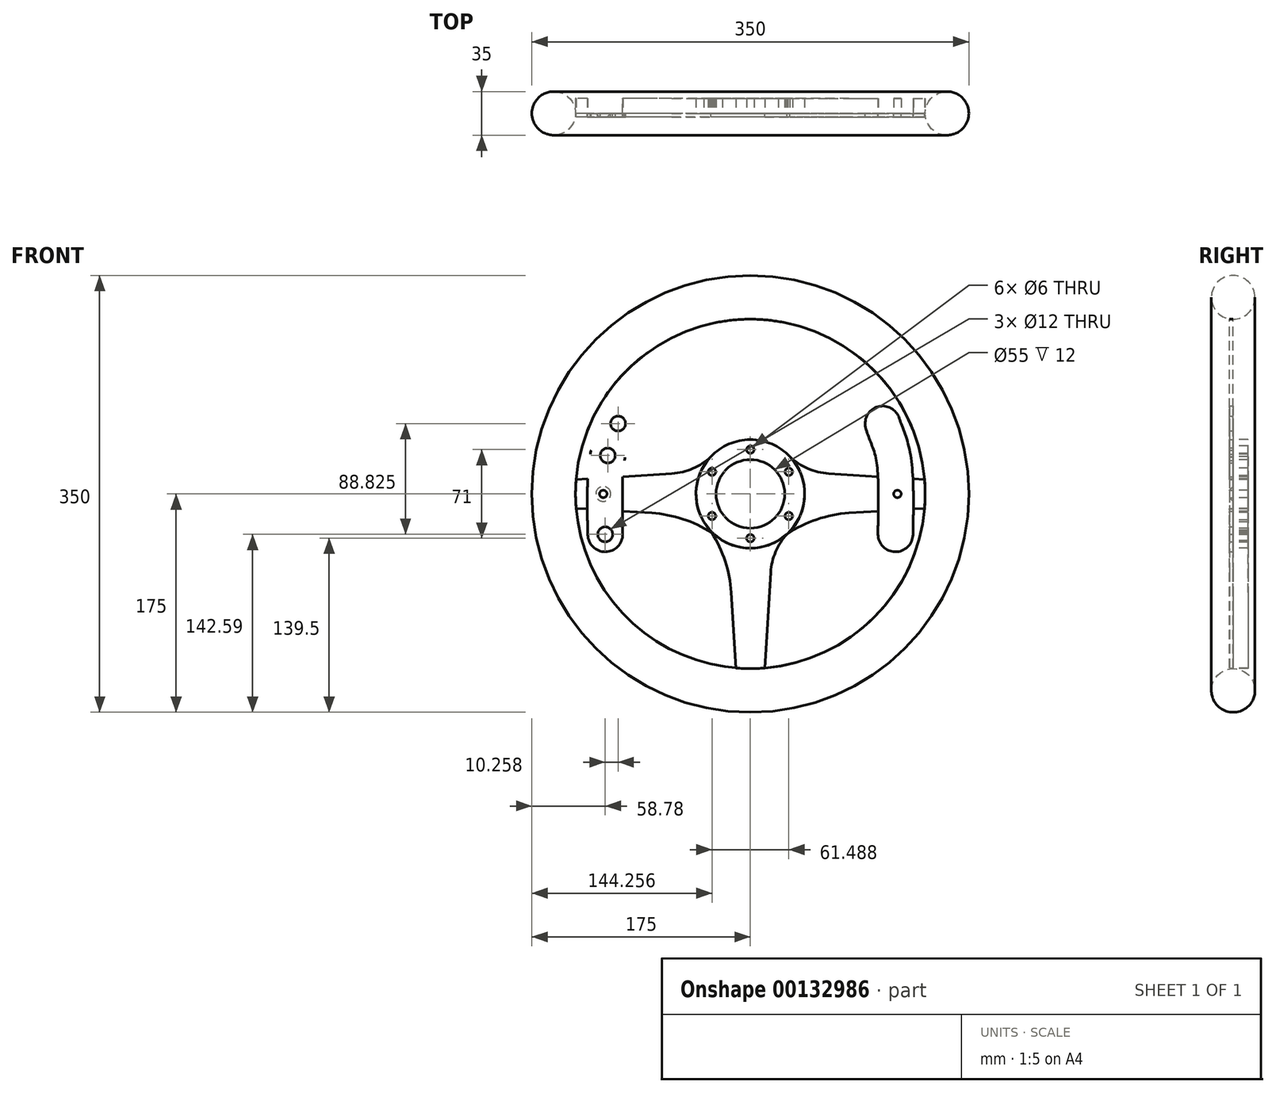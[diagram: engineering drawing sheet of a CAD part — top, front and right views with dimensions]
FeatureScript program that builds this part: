
annotation { "Feature Type Name" : "Feature", "Feature Type Description" : "" }
export const myFeature = defineFeature(function(context is Context, id is Id, definition is map)
    precondition{}
    {
        {
            var Q0;
            Q0=qCreatedBy(makeId("Front.planeOp"),FACE);
            var sketch = newSketch(context, id + "F0", { "sketchPlane" : qUnion([Q0])});
            skLineSegment(sketch, "E0", {"start": v(0, -72.3) * mm, "end": v(0, 74.64) * mm, "construction": true});
            skLineSegment(sketch, "E1", {"start": v(-80.32, 0) * mm, "end": v(78.95, 0) * mm, "construction": true});
            skCircle(sketch, "E2", {"center": v(0, 0) * mm, "radius": 175 * mm, "construction": true});
            skCircle(sketch, "E3.0", {"center": v(0, 0) * mm, "radius": 140 * mm});
            skCircle(sketch, "E4", {"center": v(0, 0) * mm, "radius": 27.5 * mm});
            skCircle(sketch, "E5.0", {"center": v(0, 0) * mm, "radius": 43.5 * mm});
            skCircle(sketch, "E6", {"center": v(0, 35.5) * mm, "radius": 3 * mm});
            skCircle(sketch, "E7.1.0", {"center": v(-30.74, 17.75) * mm, "radius": 3 * mm});
            skCircle(sketch, "E7.2.0", {"center": v(-30.74, -17.75) * mm, "radius": 3 * mm});
            skCircle(sketch, "E7.3.0", {"center": v(0, -35.5) * mm, "radius": 3 * mm});
            skCircle(sketch, "E7.4.0", {"center": v(30.74, -17.75) * mm, "radius": 3 * mm});
            skCircle(sketch, "E7.5.0", {"center": v(30.74, 17.75) * mm, "radius": 3 * mm});
            skLineSegment(sketch, "E8", {"start": v(-62.87, 16.31) * mm, "end": v(-139.52, 11.56) * mm});
            skLineSegment(sketch, "E9", {"start": v(-79.01, -15.31) * mm, "end": v(-139.52, -11.56) * mm});
            skPoint(sketch, "E10.visualSharp", {"position": v(-39.71, 17.75) * mm});
            skArc(sketch, "E10.filletArc", {"start": v(-62.87, 16.31) * mm, "mid": v(-44.9, 20.88) * mm, "end": v(-29.81, 31.68) * mm});
            skPoint(sketch, "E11.visualSharp", {"position": v(-39.71, -17.75) * mm});
            skArc(sketch, "E11.filletArc", {"start": v(-22.46, -37.25) * mm, "mid": v(-49.04, -21.9) * mm, "end": v(-79.01, -15.31) * mm});
            skArc(sketch, "E12.MirrorCS", {"start": v(62.87, 16.31) * mm, "mid": v(44.9, 20.88) * mm, "end": v(29.81, 31.68) * mm});
            skLineSegment(sketch, "E13.MirrorCS", {"start": v(62.87, 16.31) * mm, "end": v(139.52, 11.56) * mm});
            skLineSegment(sketch, "E14.MirrorCS", {"start": v(79.01, -15.31) * mm, "end": v(139.52, -11.56) * mm});
            skArc(sketch, "E15.MirrorCS", {"start": v(22.46, -37.25) * mm, "mid": v(49.04, -21.9) * mm, "end": v(79.01, -15.31) * mm});
            skLineSegment(sketch, "E16.1.0", {"start": v(16.31, -62.87) * mm, "end": v(11.56, -139.52) * mm});
            skLineSegment(sketch, "E16.1.1", {"start": v(-15.31, -79.01) * mm, "end": v(-11.56, -139.52) * mm});
            skArc(sketch, "E16.1.2", {"start": v(-37.25, -22.46) * mm, "mid": v(-21.9, -49.04) * mm, "end": v(-15.31, -79.01) * mm});
            skArc(sketch, "E16.1.3", {"start": v(16.31, -62.87) * mm, "mid": v(20.88, -44.9) * mm, "end": v(31.68, -29.81) * mm});
            skLineSegment(sketch, "E16.anchor1", {"start": v(0, 0) * mm, "end": v(62.87, 16.31) * mm, "construction": true});
            skLineSegment(sketch, "E16.anchor2", {"start": v(0, 0) * mm, "end": v(16.31, -62.87) * mm, "construction": true});
            skCircle(sketch, "E17", {"center": v(-105.96, 56.41) * mm, "radius": 6 * mm});
            skCircle(sketch, "E18", {"center": v(-114.24, 30.77) * mm, "radius": 6 * mm});
            skCircle(sketch, "E19", {"center": v(-116.22, -32.41) * mm, "radius": 6 * mm});
            skArc(sketch, "E20.0", {"start": v(-127.6, 34.93) * mm, "mid": v(-128, 33.4) * mm, "end": v(-128.2, 31.82) * mm});
            skArc(sketch, "E21.0", {"start": v(-130.22, -32.75) * mm, "mid": v(-116.05, -46.4) * mm, "end": v(-102.22, -32.4) * mm});
            skFitSpline(sketch, "E22", {"points": [v(-119.35, 60.53) * mm, v(-127.6, 34.93) * mm, v(-130.22, -32.75) * mm], "startDerivative": vector(-16, -52.1) * mm, "endDerivative": vector(2.93, -122.42) * mm});
            skFitSpline(sketch, "E23", {"points": [v(-92.33, 53.22) * mm, v(-100.31, 29.36) * mm, v(-102.22, -32.4) * mm], "startDerivative": vector(-14.72, -62.88) * mm, "endDerivative": vector(0.06, -114.96) * mm});
            skArc(sketch, "E24.trimOffspring", {"start": v(-92.33, 53.22) * mm, "mid": v(-102.3, 69.93) * mm, "end": v(-119.35, 60.53) * mm});
            skArc(sketch, "E25.trimOffspring", {"start": v(-100.81, 26.82) * mm, "mid": v(-100.5, 28.07) * mm, "end": v(-100.31, 29.36) * mm});
            skArc(sketch, "E26.MirrorCS", {"start": v(92.33, 53.22) * mm, "mid": v(102.3, 69.93) * mm, "end": v(119.35, 60.53) * mm});
            skFitSpline(sketch, "E27.MirrorCS", {"points": [v(92.33, 53.22) * mm, v(100.31, 29.36) * mm, v(102.22, -32.4) * mm], "startDerivative": vector(14.72, -62.88) * mm, "endDerivative": vector(-0.06, -114.96) * mm});
            skArc(sketch, "E28.MirrorCS", {"start": v(130.22, -32.75) * mm, "mid": v(116.05, -46.4) * mm, "end": v(102.22, -32.4) * mm});
            skFitSpline(sketch, "E29.MirrorCS", {"points": [v(119.35, 60.53) * mm, v(127.6, 34.93) * mm, v(130.22, -32.75) * mm], "startDerivative": vector(16, -52.1) * mm, "endDerivative": vector(-2.93, -122.42) * mm});
            skCircle(sketch, "E30.MirrorC", {"center": v(105.96, 56.41) * mm, "radius": 6 * mm});
            skCircle(sketch, "E31.MirrorC", {"center": v(114.24, 30.77) * mm, "radius": 6 * mm});
            skCircle(sketch, "E32.MirrorC", {"center": v(116.22, -32.41) * mm, "radius": 6 * mm});
            skCircle(sketch, "E33.MirrorC", {"center": v(117.78, 0) * mm, "radius": 3 * mm});
            skPoint(sketch, "E34", {"position": v(0, -175) * mm});
            skPoint(sketch, "E35", {"position": v(-117.78, 0) * mm});
            skSolve(sketch);
        }
        {
            var Q0;
            Q0=makeQuery(id+"F0.imprint","IMPRINT",FACE,{"disambiguationData":[TD([[makeQuery(id+"F0.imprint","IMPRINT",EDGE,{"derivedFrom":sQuery(id+"F0.wireOp",EDGE,"E17")}),-1.0]])]});
            var Q1;
            Q1=makeQuery(id+"F0.imprint","IMPRINT",FACE,{"disambiguationData":[TD([[makeQuery(id+"F0.imprint","IMPRINT",EDGE,{"derivedFrom":sQuery(id+"F0.wireOp",EDGE,"E26.MirrorCS")}),-1.0]])]});
            var Q2;
            Q2=makeQuery(id+"F0.imprint","IMPRINT",FACE,{"disambiguationData":[TD([[makeQuery(id+"F0.imprint","IMPRINT",EDGE,{"derivedFrom":sQuery(id+"F0.wireOp",EDGE,"oWARlvYR-uslC-KwjI-rm5T-suc8ZiEPwRvb")}),-1.0]])]});
            var Q3;
            Q3=makeQuery(id+"F0.imprint","IMPRINT",FACE,{"disambiguationData":[TD([[makeQuery(id+"F0.imprint","IMPRINT",EDGE,{"derivedFrom":sQuery(id+"F0.wireOp",EDGE,"E19")}),-1.0]])]});
            var Q4;
            Q4=makeQuery(id+"F0.imprint","IMPRINT",FACE,{"disambiguationData":[TD([[makeQuery(id+"F0.imprint","IMPRINT",EDGE,{"derivedFrom":sQuery(id+"F0.wireOp",EDGE,"E33.MirrorC")}),1.0]])]});
            var Q5;
            {var subQ1=sQuery(id+"F0.wireOp",EDGE,"E28.MirrorCS");Q5=makeQuery(id+"F0.imprint","IMPRINT",FACE,{"disambiguationData":[TD([[makeQuery(id+"F0.imprint","IMPRINT",EDGE,{"derivedFrom":subQ1}),-1.0]])]});}
            var Q6;
            {var subQ0=sQuery(id+"F0.wireOp",EDGE,"E23");var subQ1=sQuery(id+"F0.wireOp",EDGE,"E8");var subQ2=makeQuery(id+"F0.imprint","INTERSECT",VERTEX,{"derivedFrom":[subQ1,subQ0]});Q6=makeQuery(id+"F0.imprint","IMPRINT",FACE,{"disambiguationData":[TD([[makeQuery(id+"F0.imprint","IMPRINT",EDGE,{"disambiguationData":[TD([[subQ2,-1.0]])],"derivedFrom":subQ1}),1.0]])]});}
            extrude(context, id + "F1", {"entities" : qUnion([Q0, Q1, Q2, Q3, Q4, Q5, Q6]), "depth" : 3 * mm});
        }
        {
            var Q0;
            Q0=qCreatedBy(makeId("Right.planeOp"),FACE);
            var sketch = newSketch(context, id + "F2", { "sketchPlane" : qUnion([Q0])});
            skCircle(sketch, "E36", {"center": v(0, -157.5) * mm, "radius": 17.5 * mm});
            skPoint(sketch, "E37", {"position": v(0, -175) * mm});
            skSolve(sketch);
        }
        {
            var Q0;
            Q0=makeQuery(id+"F2.imprint","IMPRINT",FACE,{"disambiguationData":[TD([[makeQuery(id+"F2.imprint","IMPRINT",EDGE,{"derivedFrom":sQuery(id+"F2.wireOp",EDGE,"E36")}),1.0]])]});
            var Q1;
            Q1=sQuery(id+"F0.wireOp",EDGE,"E2");
            revolve(context, id + "F3", {"entities" : qUnion([Q0]), "axis" : qUnion([Q1]), "revolveType" : RevolveType.FULL});
        }
        {
            var Q0;
            {var subQ3=sQuery(id+"F0.wireOp",EDGE,"E5.0");var subQ9=sQuery(id+"F0.wireOp",EDGE,"E16.1.3");var subQ10=makeQuery(id+"F0.imprint","INTERSECT",VERTEX,{"disambiguationData":[OD(0.0)],"derivedFrom":[subQ3,subQ9]});Q0=makeQuery(id+"F0.imprint","IMPRINT",FACE,{"disambiguationData":[TD([[makeQuery(id+"F0.imprint","IMPRINT",EDGE,{"disambiguationData":[TD([[subQ10,1.0]])],"derivedFrom":subQ3}),-1.0]])]});}
            var Q1;
            {var subQ9=sQuery(id+"F0.wireOp",EDGE,"E16.1.2");var subQ10=sQuery(id+"F0.wireOp",EDGE,"E5.0");var subQ11=makeQuery(id+"F0.imprint","INTERSECT",VERTEX,{"disambiguationData":[OD(0.0)],"derivedFrom":[subQ10,subQ9]});Q1=makeQuery(id+"F0.imprint","IMPRINT",FACE,{"disambiguationData":[TD([[makeQuery(id+"F0.imprint","IMPRINT",EDGE,{"disambiguationData":[TD([[subQ11,1.0]])],"derivedFrom":subQ10}),-1.0]])]});}
            var Q2;
            {var subQ10=sQuery(id+"F0.wireOp",EDGE,"E16.1.0");Q2=makeQuery(id+"F0.imprint","IMPRINT",FACE,{"disambiguationData":[TD([[makeQuery(id+"F0.imprint","IMPRINT",EDGE,{"derivedFrom":subQ10}),-1.0]])]});}
            var Q3;
            {var subQ0=sQuery(id+"F0.wireOp",EDGE,"E8");var subQ1=sQuery(id+"F0.wireOp",EDGE,"E3.0");var subQ2=makeQuery(id+"F0.imprint","INTERSECT",VERTEX,{"derivedFrom":[subQ1,subQ0]});Q3=makeQuery(id+"F0.imprint","IMPRINT",FACE,{"disambiguationData":[TD([[makeQuery(id+"F0.imprint","IMPRINT",EDGE,{"disambiguationData":[TD([[subQ2,-1.0]])],"derivedFrom":subQ1}),1.0]])]});}
            var Q4;
            Q4=makeQuery(id+"F0.imprint","IMPRINT",FACE,{"disambiguationData":[TD([[makeQuery(id+"F0.imprint","IMPRINT",EDGE,{"derivedFrom":sQuery(id+"F0.wireOp",EDGE,"oWARlvYR-uslC-KwjI-rm5T-suc8ZiEPwRvb")}),-1.0]])]});
            var Q5;
            Q5=makeQuery(id+"F0.imprint","IMPRINT",FACE,{"disambiguationData":[TD([[makeQuery(id+"F0.imprint","IMPRINT",EDGE,{"derivedFrom":sQuery(id+"F0.wireOp",EDGE,"E33.MirrorC")}),1.0]])]});
            var Q6;
            {var subQ0=sQuery(id+"F0.wireOp",EDGE,"E13.MirrorCS");var subQ1=sQuery(id+"F0.wireOp",EDGE,"E3.0");var subQ2=makeQuery(id+"F0.imprint","INTERSECT",VERTEX,{"derivedFrom":[subQ1,subQ0]});Q6=makeQuery(id+"F0.imprint","IMPRINT",FACE,{"disambiguationData":[TD([[makeQuery(id+"F0.imprint","IMPRINT",EDGE,{"disambiguationData":[TD([[subQ2,1.0]])],"derivedFrom":subQ1}),1.0]])]});}
            extrude(context, id + "F4", {"entities" : qUnion([Q0, Q1, Q2, Q3, Q4, Q5, Q6]), "oppositeDirection" : true, "depth" : 12 * mm});
        }
        {
            var Q0;
            Q0=makeQuery(id+"F0.imprint","IMPRINT",FACE,{"disambiguationData":[TD([[makeQuery(id+"F0.imprint","IMPRINT",EDGE,{"derivedFrom":sQuery(id+"F0.wireOp",EDGE,"E4")}),-1.0]])]});
            extrude(context, id + "F5", {"entities" : qUnion([Q0]), "oppositeDirection" : true, "depth" : 12 * mm});
        }
        {
            var Q0;
            Q0=sQuery(id+"F0.wireOp",VERTEX,"E35");
            var Q1;
            Q1=makeQuery(id+"F1.opExtrude","SWEPT_BODY",BODY,{"disambiguationData":[OSD([sQuery(id+"F0.wireOp",EDGE,"E17"),sQuery(id+"F0.wireOp",EDGE,"E18"),sQuery(id+"F0.wireOp",EDGE,"E19"),sQuery(id+"F0.wireOp",EDGE,"E21.0"),sQuery(id+"F0.wireOp",EDGE,"E22"),sQuery(id+"F0.wireOp",EDGE,"E23"),sQuery(id+"F0.wireOp",EDGE,"E24.trimOffspring")])]});
            hole(context, id + "F6", {"style" : HoleStyle.C_SINK, "endStyle" : HoleEndStyle.THROUGH, "oppositeDirection" : true, "holeDiameter" : 6 * mm, "cSinkDiameter" : 12 * mm, "cSinkAngle" : 90 * degree, "locations" : qUnion([Q0]), "scope" : qUnion([Q1]), "isTappedThrough" : true});
        }
    });
